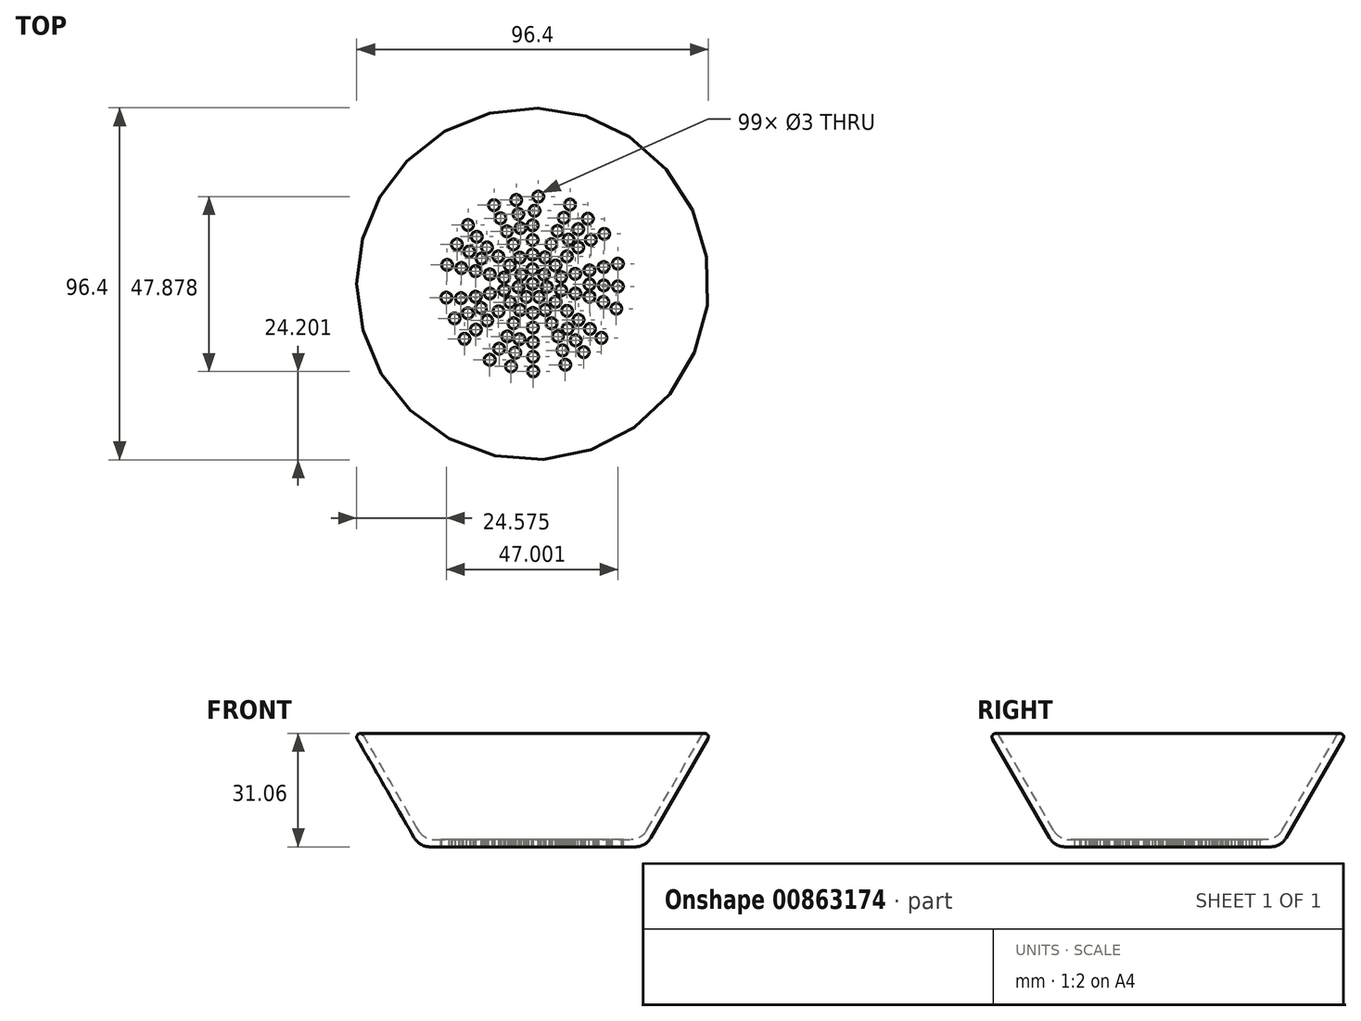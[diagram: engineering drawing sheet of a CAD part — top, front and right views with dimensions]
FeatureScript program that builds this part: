
annotation { "Feature Type Name" : "Feature", "Feature Type Description" : "" }
export const myFeature = defineFeature(function(context is Context, id is Id, definition is map)
    precondition{}
    {
        {
            var Q0;
            Q0=qCreatedBy(makeId("Front.planeOp"),FACE);
            var sketch = newSketch(context, id + "F0", { "sketchPlane" : qUnion([Q0])});
            skLineSegment(sketch, "E0", {"start": v(0, 0) * mm, "end": v(26.96, 0) * mm});
            skLineSegment(sketch, "E1", {"start": v(31.29, 2.5) * mm, "end": v(46.33, 28.56) * mm});
            skLineSegment(sketch, "E2.0", {"start": v(32.44, 0.5) * mm, "end": v(48.06, 27.56) * mm});
            skLineSegment(sketch, "E2.1", {"start": v(0, -2) * mm, "end": v(28.11, -2) * mm});
            skLineSegment(sketch, "E3", {"start": v(47.81, 28.85) * mm, "end": v(47.81, 28.85) * mm});
            skLineSegment(sketch, "E4", {"start": v(0, -2) * mm, "end": v(0, 47.87) * mm});
            skPoint(sketch, "E5.visualSharp", {"position": v(31, -2) * mm});
            skArc(sketch, "E5.filletArc", {"start": v(28.11, -2) * mm, "mid": v(30.61, -1.33) * mm, "end": v(32.44, 0.5) * mm});
            skPoint(sketch, "E6.visualSharp", {"position": v(29.85, 0) * mm});
            skArc(sketch, "E6.filletArc", {"start": v(26.96, 0) * mm, "mid": v(29.46, 0.67) * mm, "end": v(31.29, 2.5) * mm});
            skPoint(sketch, "E7.visualSharp", {"position": v(48.5, 28.31) * mm});
            skArc(sketch, "E7.filletArc", {"start": v(48.06, 27.56) * mm, "mid": v(48.18, 28.25) * mm, "end": v(47.81, 28.85) * mm});
            skPoint(sketch, "E8.visualSharp", {"position": v(46.9, 29.55) * mm});
            skArc(sketch, "E8.filletArc", {"start": v(47.81, 28.85) * mm, "mid": v(47, 29.04) * mm, "end": v(46.33, 28.56) * mm});
            skSolve(sketch);
        }
        {
            var Q0;
            Q0=qSketchRegion(id+"F0",true);
            var Q1;
            Q1=sQuery(id+"F0.wireOp",EDGE,"E4");
            revolve(context, id + "F1", {"surfaceOperationType" : NewSurfaceOperationType.NEW, "entities" : qUnion([Q0]), "axis" : qUnion([Q1]), "revolveType" : RevolveType.FULL});
        }
        {
            var Q0;
            Q0=makeQuery(id+"F1.opRevolve","SWEPT_FACE",FACE,{"disambiguationData":[OSD([sQuery(id+"F0.wireOp",EDGE,"E0")])]});
            var sketch = newSketch(context, id + "F2", { "sketchPlane" : qUnion([Q0])});
            skCircle(sketch, "E9", {"center": v(0.54, 20.01) * mm, "radius": 1.5 * mm});
            skCircle(sketch, "E10", {"center": v(0, 16.01) * mm, "radius": 1.5 * mm});
            skCircle(sketch, "E11", {"center": v(0, 12.01) * mm, "radius": 1.5 * mm});
            skCircle(sketch, "E12", {"center": v(0, 8.01) * mm, "radius": 1.5 * mm});
            skCircle(sketch, "E13", {"center": v(-0.02, 4.01) * mm, "radius": 1.5 * mm});
            skCircle(sketch, "E14", {"center": v(1.55, 23.88) * mm, "radius": 1.5 * mm});
            skCircle(sketch, "E15.1.0", {"center": v(-3.15, 2.48) * mm, "radius": 1.5 * mm});
            skCircle(sketch, "E15.1.1", {"center": v(-9.39, 7.49) * mm, "radius": 1.5 * mm});
            skCircle(sketch, "E15.1.2", {"center": v(-6.26, 5) * mm, "radius": 1.5 * mm});
            skCircle(sketch, "E15.1.3", {"center": v(-12.52, 9.98) * mm, "radius": 1.5 * mm});
            skCircle(sketch, "E15.1.4", {"center": v(-15.31, 12.9) * mm, "radius": 1.5 * mm});
            skCircle(sketch, "E15.1.5", {"center": v(-17.7, 16.1) * mm, "radius": 1.5 * mm});
            skCircle(sketch, "E15.2.0", {"center": v(-3.9, -0.91) * mm, "radius": 1.5 * mm});
            skCircle(sketch, "E15.2.1", {"center": v(-11.7, -2.67) * mm, "radius": 1.5 * mm});
            skCircle(sketch, "E15.2.2", {"center": v(-7.8, -1.78) * mm, "radius": 1.5 * mm});
            skCircle(sketch, "E15.2.3", {"center": v(-15.6, -3.56) * mm, "radius": 1.5 * mm});
            skCircle(sketch, "E15.2.4", {"center": v(-19.63, -3.93) * mm, "radius": 1.5 * mm});
            skCircle(sketch, "E15.2.5", {"center": v(-23.63, -3.8) * mm, "radius": 1.5 * mm});
            skPoint(sketch, "E15.center", {"position": v(0, 0) * mm});
            skCircle(sketch, "E16.1.3.0", {"center": v(-1.72, -3.62) * mm, "radius": 1.5 * mm});
            skCircle(sketch, "E16.2.3.0", {"center": v(-5.21, -10.82) * mm, "radius": 1.5 * mm});
            skCircle(sketch, "E16.4.3.0", {"center": v(-3.48, -7.22) * mm, "radius": 1.5 * mm});
            skCircle(sketch, "E16.6.3.0", {"center": v(-6.95, -14.42) * mm, "radius": 1.5 * mm});
            skCircle(sketch, "E16.8.3.0", {"center": v(-9.16, -17.8) * mm, "radius": 1.5 * mm});
            skCircle(sketch, "E16.10.3.0", {"center": v(-11.76, -20.84) * mm, "radius": 1.5 * mm});
            skCircle(sketch, "E16.1.4.0", {"center": v(1.76, -3.6) * mm, "radius": 1.5 * mm});
            skCircle(sketch, "E16.2.4.0", {"center": v(5.21, -10.82) * mm, "radius": 1.5 * mm});
            skCircle(sketch, "E16.4.4.0", {"center": v(3.48, -7.22) * mm, "radius": 1.5 * mm});
            skCircle(sketch, "E16.6.4.0", {"center": v(6.95, -14.42) * mm, "radius": 1.5 * mm});
            skCircle(sketch, "E16.8.4.0", {"center": v(8.2, -18.26) * mm, "radius": 1.5 * mm});
            skCircle(sketch, "E16.10.4.0", {"center": v(8.96, -22.19) * mm, "radius": 1.5 * mm});
            skCircle(sketch, "E16.1.5.0", {"center": v(3.91, -0.87) * mm, "radius": 1.5 * mm});
            skCircle(sketch, "E16.2.5.0", {"center": v(11.7, -2.67) * mm, "radius": 1.5 * mm});
            skCircle(sketch, "E16.4.5.0", {"center": v(7.8, -1.78) * mm, "radius": 1.5 * mm});
            skCircle(sketch, "E16.6.5.0", {"center": v(15.6, -3.56) * mm, "radius": 1.5 * mm});
            skCircle(sketch, "E16.8.5.0", {"center": v(19.39, -4.97) * mm, "radius": 1.5 * mm});
            skCircle(sketch, "E16.10.5.0", {"center": v(22.93, -6.83) * mm, "radius": 1.5 * mm});
            skCircle(sketch, "E16.1.6.0", {"center": v(3.12, 2.52) * mm, "radius": 1.5 * mm});
            skCircle(sketch, "E16.2.6.0", {"center": v(9.39, 7.49) * mm, "radius": 1.5 * mm});
            skCircle(sketch, "E16.4.6.0", {"center": v(6.26, 5) * mm, "radius": 1.5 * mm});
            skCircle(sketch, "E16.6.6.0", {"center": v(12.52, 9.98) * mm, "radius": 1.5 * mm});
            skCircle(sketch, "E16.8.6.0", {"center": v(15.98, 12.06) * mm, "radius": 1.5 * mm});
            skCircle(sketch, "E16.10.6.0", {"center": v(19.64, 13.67) * mm, "radius": 1.5 * mm});
            skLineSegment(sketch, "E17", {"start": v(0, 0) * mm, "end": v(-20.96, -16.95) * mm});
            skLineSegment(sketch, "E18", {"start": v(-23.63, -3.8) * mm, "end": v(-11.76, -20.84) * mm});
            skCircle(sketch, "E19", {"center": v(-6.22, -5.03) * mm, "radius": 1.5 * mm});
            skCircle(sketch, "E20", {"center": v(-9.33, -7.54) * mm, "radius": 1.5 * mm});
            skCircle(sketch, "E21", {"center": v(-12.44, -10.06) * mm, "radius": 1.5 * mm});
            skCircle(sketch, "E22", {"center": v(-15.55, -12.57) * mm, "radius": 1.5 * mm});
            skCircle(sketch, "E23", {"center": v(-18.66, -15.09) * mm, "radius": 1.5 * mm});
            skCircle(sketch, "E24.1.0", {"center": v(0.16, -24) * mm, "radius": 1.5 * mm});
            skCircle(sketch, "E24.1.1", {"center": v(0.13, -20) * mm, "radius": 1.5 * mm});
            skCircle(sketch, "E24.1.2", {"center": v(0.1, -16) * mm, "radius": 1.5 * mm});
            skCircle(sketch, "E24.1.3", {"center": v(0.08, -12) * mm, "radius": 1.5 * mm});
            skCircle(sketch, "E24.1.4", {"center": v(0.05, -8) * mm, "radius": 1.5 * mm});
            skCircle(sketch, "E24.2.0", {"center": v(18.86, -14.84) * mm, "radius": 1.5 * mm});
            skCircle(sketch, "E24.2.1", {"center": v(15.72, -12.36) * mm, "radius": 1.5 * mm});
            skCircle(sketch, "E24.2.2", {"center": v(12.58, -9.9) * mm, "radius": 1.5 * mm});
            skCircle(sketch, "E24.2.3", {"center": v(9.43, -7.42) * mm, "radius": 1.5 * mm});
            skCircle(sketch, "E24.2.4", {"center": v(6.29, -4.95) * mm, "radius": 1.5 * mm});
            skCircle(sketch, "E25.1.3.0", {"center": v(23.36, 5.5) * mm, "radius": 1.5 * mm});
            skCircle(sketch, "E25.2.3.0", {"center": v(19.47, 4.58) * mm, "radius": 1.5 * mm});
            skCircle(sketch, "E25.4.3.0", {"center": v(15.57, 3.67) * mm, "radius": 1.5 * mm});
            skCircle(sketch, "E25.6.3.0", {"center": v(11.68, 2.75) * mm, "radius": 1.5 * mm});
            skCircle(sketch, "E25.8.3.0", {"center": v(7.79, 1.83) * mm, "radius": 1.5 * mm});
            skCircle(sketch, "E25.1.4.0", {"center": v(10.27, 21.7) * mm, "radius": 1.5 * mm});
            skCircle(sketch, "E25.2.4.0", {"center": v(8.56, 18.08) * mm, "radius": 1.5 * mm});
            skCircle(sketch, "E25.4.4.0", {"center": v(6.84, 14.46) * mm, "radius": 1.5 * mm});
            skCircle(sketch, "E25.6.4.0", {"center": v(5.13, 10.85) * mm, "radius": 1.5 * mm});
            skCircle(sketch, "E25.8.4.0", {"center": v(3.42, 7.23) * mm, "radius": 1.5 * mm});
            skCircle(sketch, "E25.1.5.0", {"center": v(-10.56, 21.55) * mm, "radius": 1.5 * mm});
            skCircle(sketch, "E25.2.5.0", {"center": v(-8.8, 17.96) * mm, "radius": 1.5 * mm});
            skCircle(sketch, "E25.4.5.0", {"center": v(-7.04, 14.37) * mm, "radius": 1.5 * mm});
            skCircle(sketch, "E25.6.5.0", {"center": v(-5.28, 10.78) * mm, "radius": 1.5 * mm});
            skCircle(sketch, "E25.8.5.0", {"center": v(-3.52, 7.18) * mm, "radius": 1.5 * mm});
            skCircle(sketch, "E25.1.6.0", {"center": v(-23.43, 5.18) * mm, "radius": 1.5 * mm});
            skCircle(sketch, "E25.2.6.0", {"center": v(-19.53, 4.32) * mm, "radius": 1.5 * mm});
            skCircle(sketch, "E25.4.6.0", {"center": v(-15.62, 3.46) * mm, "radius": 1.5 * mm});
            skCircle(sketch, "E25.6.6.0", {"center": v(-11.72, 2.6) * mm, "radius": 1.5 * mm});
            skCircle(sketch, "E25.8.6.0", {"center": v(-7.81, 1.73) * mm, "radius": 1.5 * mm});
            skCircle(sketch, "E26", {"center": v(0, 0) * mm, "radius": 1.5 * mm});
            skSolve(sketch);
        }
        {
            var Q0;
            Q0 = qSketchRegion(id + "F2", true);
            extrude(context, id + "F3", {"entities" : qUnion([Q0]), "operationType" : NewBodyOperationType.REMOVE, "oppositeDirection" : true, "depth" : 25 * mm, "offsetDistance" : 25 * mm});
        }
        {
            var Q0;
            Q0=makeQuery(id+"F1.opRevolve","SWEPT_FACE",FACE,{"disambiguationData":[OSD([sQuery(id+"F0.wireOp",EDGE,"E0")])]});
            var sketch = newSketch(context, id + "F4", { "sketchPlane" : qUnion([Q0])});
            skLineSegment(sketch, "E27", {"start": v(-24.66, -10.89) * mm, "end": v(-10.5, -5.15) * mm});
            skLineSegment(sketch, "E28", {"start": v(-9.33, -7.54) * mm, "end": v(-11.7, -2.67) * mm});
            skLineSegment(sketch, "E29", {"start": v(-18.66, -15.09) * mm, "end": v(-23.63, -3.8) * mm});
            skCircle(sketch, "E30", {"center": v(-14.12, -6.61) * mm, "radius": 1.5 * mm});
            skCircle(sketch, "E31", {"center": v(-17.75, -8.06) * mm, "radius": 1.5 * mm});
            skCircle(sketch, "E32", {"center": v(-21.38, -9.49) * mm, "radius": 1.5 * mm});
            skCircle(sketch, "E33.1.0", {"center": v(-4.76, -18.9) * mm, "radius": 1.5 * mm});
            skCircle(sketch, "E33.1.1", {"center": v(-3.63, -15.17) * mm, "radius": 1.5 * mm});
            skCircle(sketch, "E33.1.2", {"center": v(-5.91, -22.63) * mm, "radius": 1.5 * mm});
            skCircle(sketch, "E33.2.0", {"center": v(11.8, -15.5) * mm, "radius": 1.5 * mm});
            skCircle(sketch, "E33.2.1", {"center": v(9.6, -12.3) * mm, "radius": 1.5 * mm});
            skCircle(sketch, "E33.2.2", {"center": v(14, -18.73) * mm, "radius": 1.5 * mm});
            skCircle(sketch, "E33.3.0", {"center": v(19.49, -0.44) * mm, "radius": 1.5 * mm});
            skCircle(sketch, "E33.3.1", {"center": v(15.6, -0.17) * mm, "radius": 1.5 * mm});
            skCircle(sketch, "E33.3.2", {"center": v(23.38, -0.73) * mm, "radius": 1.5 * mm});
            skCircle(sketch, "E33.4.0", {"center": v(12.5, 14.96) * mm, "radius": 1.5 * mm});
            skCircle(sketch, "E33.4.1", {"center": v(9.86, 12.09) * mm, "radius": 1.5 * mm});
            skCircle(sketch, "E33.4.2", {"center": v(15.14, 17.82) * mm, "radius": 1.5 * mm});
            skCircle(sketch, "E33.5.0", {"center": v(-3.9, 19.1) * mm, "radius": 1.5 * mm});
            skCircle(sketch, "E33.5.1", {"center": v(-3.3, 15.24) * mm, "radius": 1.5 * mm});
            skCircle(sketch, "E33.5.2", {"center": v(-4.5, 22.95) * mm, "radius": 1.5 * mm});
            skCircle(sketch, "E33.6.0", {"center": v(-17.37, 8.85) * mm, "radius": 1.5 * mm});
            skCircle(sketch, "E33.6.1", {"center": v(-13.98, 6.92) * mm, "radius": 1.5 * mm});
            skCircle(sketch, "E33.6.2", {"center": v(-20.74, 10.8) * mm, "radius": 1.5 * mm});
            skPoint(sketch, "E33.center", {"position": v(0, 0) * mm});
            skSolve(sketch);
        }
        {
            var Q0;
            Q0 = qSketchRegion(id + "F4", true);
            extrude(context, id + "F5", {"entities" : qUnion([Q0]), "operationType" : NewBodyOperationType.REMOVE, "oppositeDirection" : true, "depth" : 25 * mm, "offsetDistance" : 25 * mm});
        }
    });
